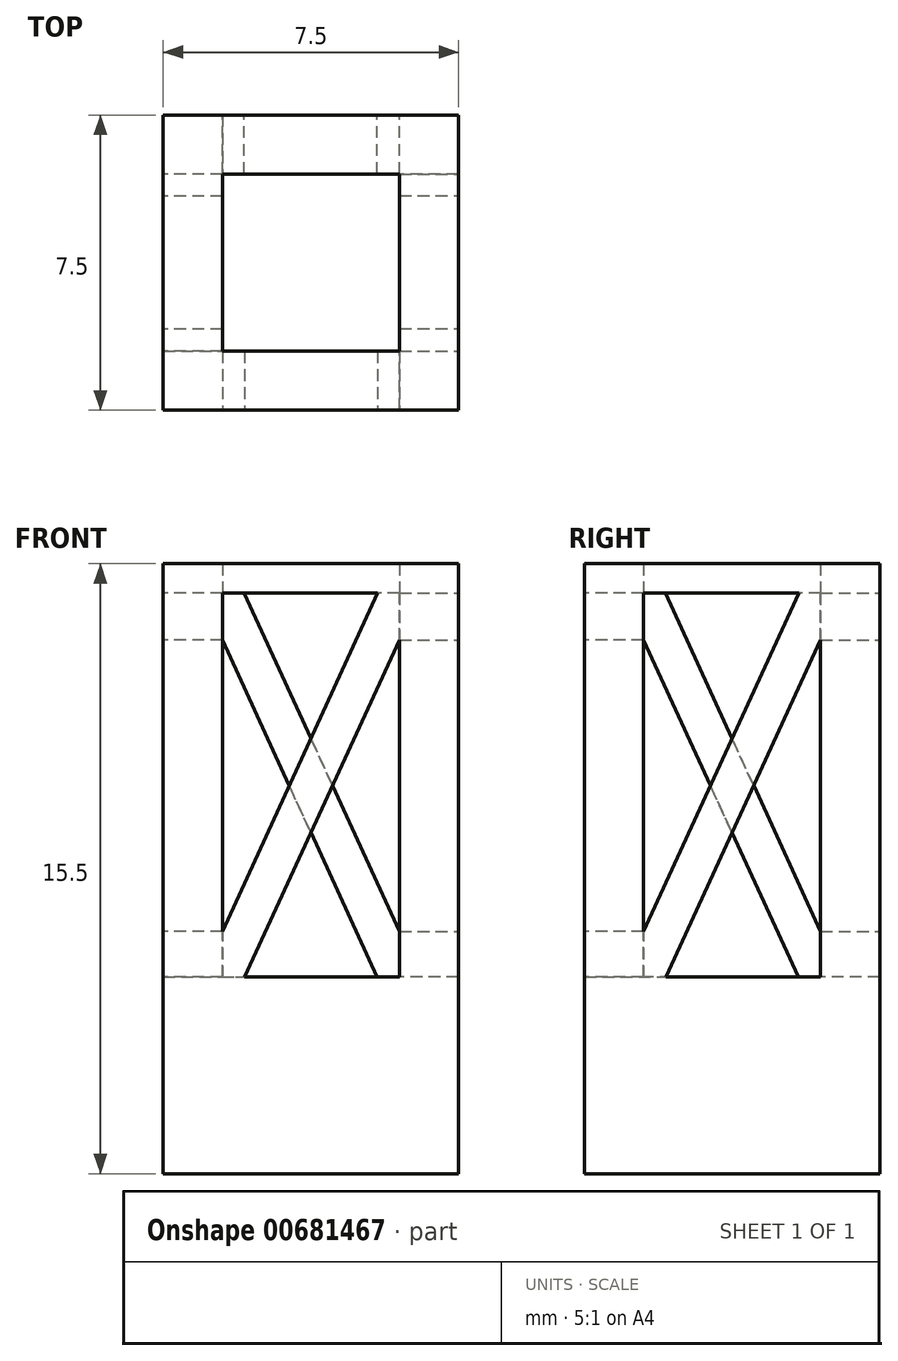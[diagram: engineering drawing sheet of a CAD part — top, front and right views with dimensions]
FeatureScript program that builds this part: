
annotation { "Feature Type Name" : "Feature", "Feature Type Description" : "" }
export const myFeature = defineFeature(function(context is Context, id is Id, definition is map)
    precondition{}
    {
        {
            var Q0;
            Q0=qCreatedBy(makeId("Top.planeOp"),FACE);
            var sketch = newSketch(context, id + "F0", { "sketchPlane" : qUnion([Q0])});
            skLineSegment(sketch, "E0.bottom", {"start": v(-38.75, 50) * mm, "end": v(-31.25, 50) * mm});
            skPoint(sketch, "E0.middle", {"position": v(0, 0) * mm});
            skLineSegment(sketch, "E1.top", {"start": v(-38.75, 42.5) * mm, "end": v(-31.25, 42.5) * mm});
            skLineSegment(sketch, "E1.left", {"start": v(-38.75, 50) * mm, "end": v(-38.75, 42.5) * mm});
            skLineSegment(sketch, "E1.right", {"start": v(-31.25, 50) * mm, "end": v(-31.25, 42.5) * mm});
            skLineSegment(sketch, "E2.bottom", {"start": v(38.75, 50) * mm, "end": v(31.25, 50) * mm});
            skLineSegment(sketch, "E3.trimOffspring", {"start": v(31.25, 50) * mm, "end": v(38.75, 50) * mm});
            skLineSegment(sketch, "E4", {"start": v(-38.75, 50) * mm, "end": v(38.75, 50) * mm});
            skLineSegment(sketch, "E5", {"start": v(-38.75, 50) * mm, "end": v(-38.75, -50) * mm});
            skPoint(sketch, "E5.endSnap0", {"position": v(-38.75, 46.25) * mm});
            skSolve(sketch);
        }
        {
            var Q0;
            {var subQ0=sQuery(id+"F0.wireOp",EDGE,"E1.top");Q0=makeQuery(id+"F0.imprint","IMPRINT",FACE,{"disambiguationData":[TD([[makeQuery(id+"F0.imprint","IMPRINT",EDGE,{"derivedFrom":subQ0}),1.0]])]});}
            extrude(context, id + "F1", {"entities" : qUnion([Q0]), "depth" : 5 * mm, "offsetDistance" : 25 * mm});
        }
        {
            var Q0;
            Q0=makeQuery(id+"F1.opExtrude","CAP_FACE",FACE,{"disambiguationData":[OSD([sQuery(id+"F0.wireOp",EDGE,"E0.bottom"),sQuery(id+"F0.wireOp",EDGE,"E1.top"),sQuery(id+"F0.wireOp",EDGE,"E1.left"),sQuery(id+"F0.wireOp",EDGE,"E1.right")])],"isStart":false});
            var sketch = newSketch(context, id + "F2", { "sketchPlane" : qUnion([Q0])});
            skLineSegment(sketch, "E6.bottom", {"start": v(-38.75, 50) * mm, "end": v(-37.25, 50) * mm});
            skLineSegment(sketch, "E6.top", {"start": v(-38.75, 48.5) * mm, "end": v(-37.25, 48.5) * mm});
            skLineSegment(sketch, "E6.left", {"start": v(-38.75, 50) * mm, "end": v(-38.75, 48.5) * mm});
            skLineSegment(sketch, "E6.right", {"start": v(-37.25, 50) * mm, "end": v(-37.25, 48.5) * mm});
            skLineSegment(sketch, "E7.bottom", {"start": v(-31.25, 42.5) * mm, "end": v(-32.75, 42.5) * mm});
            skLineSegment(sketch, "E8.bottom", {"start": v(-38.75, 42.5) * mm, "end": v(-37.25, 42.5) * mm});
            skLineSegment(sketch, "E8.top", {"start": v(-38.75, 44) * mm, "end": v(-37.25, 44) * mm});
            skLineSegment(sketch, "E8.left", {"start": v(-38.75, 42.5) * mm, "end": v(-38.75, 44) * mm});
            skLineSegment(sketch, "E8.right", {"start": v(-37.25, 42.5) * mm, "end": v(-37.25, 44) * mm});
            skLineSegment(sketch, "E9.top", {"start": v(-31.25, 44) * mm, "end": v(-32.75, 44) * mm});
            skLineSegment(sketch, "E9.left", {"start": v(-31.25, 42.5) * mm, "end": v(-31.25, 44) * mm});
            skLineSegment(sketch, "E9.right", {"start": v(-32.75, 42.5) * mm, "end": v(-32.75, 44) * mm});
            skLineSegment(sketch, "E10.bottom", {"start": v(-31.25, 50) * mm, "end": v(-32.75, 50) * mm});
            skLineSegment(sketch, "E10.top", {"start": v(-31.25, 48.5) * mm, "end": v(-32.75, 48.5) * mm});
            skLineSegment(sketch, "E10.left", {"start": v(-31.25, 50) * mm, "end": v(-31.25, 48.5) * mm});
            skLineSegment(sketch, "E10.right", {"start": v(-32.75, 50) * mm, "end": v(-32.75, 48.5) * mm});
            skSolve(sketch);
        }
        {
            var Q0;
            Q0=qSketchRegion(id+"F2",true);
            extrude(context, id + "F3", {"entities" : qUnion([Q0]), "operationType" : NewBodyOperationType.ADD, "depth" : 45 * mm, "offsetDistance" : 25 * mm});
        }
        {
            var Q0;
            Q0=makeQuery(id+"F3.opExtrude","CAP_FACE",FACE,{"disambiguationData":[OSD([sQuery(id+"F2.wireOp",EDGE,"E6.bottom"),sQuery(id+"F2.wireOp",EDGE,"E6.top"),sQuery(id+"F2.wireOp",EDGE,"E6.left"),sQuery(id+"F2.wireOp",EDGE,"E6.right")])],"isStart":false});
            var sketch = newSketch(context, id + "F4", { "sketchPlane" : qUnion([Q0])});
            skLineSegment(sketch, "E11.bottom", {"start": v(-38.75, 50) * mm, "end": v(-31.25, 50) * mm});
            skLineSegment(sketch, "E11.top", {"start": v(-38.75, 42.5) * mm, "end": v(-31.25, 42.5) * mm});
            skLineSegment(sketch, "E11.left", {"start": v(-38.75, 50) * mm, "end": v(-38.75, 42.5) * mm});
            skLineSegment(sketch, "E11.right", {"start": v(-31.25, 50) * mm, "end": v(-31.25, 42.5) * mm});
            skSolve(sketch);
        }
        {
            var Q0;
            Q0=qSketchRegion(id+"F4",true);
            extrude(context, id + "F5", {"entities" : qUnion([Q0]), "operationType" : NewBodyOperationType.ADD, "depth" : 5 * mm, "offsetDistance" : 25 * mm});
        }
        {
            var Q0;
            Q0=makeQuery(id+"F5.boolean.opBoolean","MERGE",FACE,{"derivedFrom":[makeQuery(id+"F3.boolean.opBoolean","MERGE",FACE,{"derivedFrom":[makeQuery(id+"F1.opExtrude","SWEPT_FACE",FACE,{"disambiguationData":[OSD([sQuery(id+"F0.wireOp",EDGE,"E1.left")])]}),makeQuery(id+"F3.opExtrude","SWEPT_FACE",FACE,{"disambiguationData":[OSD([sQuery(id+"F2.wireOp",EDGE,"E6.left")])]}),makeQuery(id+"F3.opExtrude","SWEPT_FACE",FACE,{"disambiguationData":[OSD([sQuery(id+"F2.wireOp",EDGE,"E8.left")])]})]}),makeQuery(id+"F5.opExtrude","SWEPT_FACE",FACE,{"disambiguationData":[OSD([sQuery(id+"F4.wireOp",EDGE,"E11.left")])]})]});
            var sketch = newSketch(context, id + "F6", { "sketchPlane" : qUnion([Q0])});
            skLineSegment(sketch, "E12", {"start": v(-48.5, 5) * mm, "end": v(-48.5, 14.75) * mm});
            skLineSegment(sketch, "E13", {"start": v(-48.5, 14.75) * mm, "end": v(-48.5, 16.75) * mm});
            skLineSegment(sketch, "E14", {"start": v(-48.5, 16.75) * mm, "end": v(-48.5, 26.5) * mm});
            skLineSegment(sketch, "E15", {"start": v(-48.5, 26.5) * mm, "end": v(-48.5, 28.5) * mm});
            skLineSegment(sketch, "E16", {"start": v(-48.5, 28.5) * mm, "end": v(-48.5, 38.25) * mm});
            skLineSegment(sketch, "E17", {"start": v(-48.5, 38.25) * mm, "end": v(-48.5, 40.25) * mm});
            skLineSegment(sketch, "E18", {"start": v(-48.5, 40.25) * mm, "end": v(-48.5, 50) * mm});
            skLineSegment(sketch, "E19", {"start": v(-48.5, 40.25) * mm, "end": v(-44.57, 40.25) * mm});
            skLineSegment(sketch, "E20", {"start": v(-48.5, 38.25) * mm, "end": v(-44.55, 38.25) * mm});
            skLineSegment(sketch, "E21", {"start": v(-47.96, 28.5) * mm, "end": v(-44, 28.5) * mm});
            skLineSegment(sketch, "E22", {"start": v(-48.5, 26.5) * mm, "end": v(-48.49, 26.5) * mm});
            skLineSegment(sketch, "E23", {"start": v(-48.5, 16.75) * mm, "end": v(-44.58, 16.75) * mm});
            skLineSegment(sketch, "E24", {"start": v(-48.5, 14.75) * mm, "end": v(-44.55, 14.75) * mm});
            skLineSegment(sketch, "E25.bottom", {"start": v(-48.5, 6.16) * mm, "end": v(-44.4, 15.08) * mm});
            skLineSegment(sketch, "E25.top", {"start": v(-47.93, 5) * mm, "end": v(-43.5, 14.66) * mm});
            skLineSegment(sketch, "E25.right", {"start": v(-44, 14.9) * mm, "end": v(-43.5, 14.66) * mm});
            skLineSegment(sketch, "E26", {"start": v(-43.95, 14.87) * mm, "end": v(-44, 14.76) * mm});
            skLineSegment(sketch, "E27.bottom", {"start": v(-44.45, 16.47) * mm, "end": v(-49.03, 26.47) * mm});
            skLineSegment(sketch, "E27.top", {"start": v(-43.54, 16.89) * mm, "end": v(-47.94, 26.5) * mm});
            skLineSegment(sketch, "E27.left", {"start": v(-44, 16.67) * mm, "end": v(-43.54, 16.89) * mm});
            skLineSegment(sketch, "E27.right", {"start": v(-48.57, 26.68) * mm, "end": v(-48.12, 26.89) * mm});
            skLineSegment(sketch, "E28", {"start": v(-44, 16.68) * mm, "end": v(-44, 16.7) * mm});
            skLineSegment(sketch, "E29", {"start": v(-48.57, 26.68) * mm, "end": v(-47.42, 24.16) * mm});
            skLineSegment(sketch, "E30.bottom", {"start": v(-49.02, 28.6) * mm, "end": v(-44.55, 38.25) * mm});
            skLineSegment(sketch, "E30.top", {"start": v(-47.96, 28.5) * mm, "end": v(-43.5, 38.16) * mm});
            skLineSegment(sketch, "E30.left", {"start": v(-49.02, 28.6) * mm, "end": v(-48.1, 28.18) * mm});
            skLineSegment(sketch, "E30.right", {"start": v(-44.4, 38.58) * mm, "end": v(-43.5, 38.16) * mm});
            skLineSegment(sketch, "E31", {"start": v(-48.56, 28.39) * mm, "end": v(-47.84, 29.96) * mm});
            skLineSegment(sketch, "E32", {"start": v(-43.94, 38.37) * mm, "end": v(-45.1, 35.86) * mm});
            skLineSegment(sketch, "E33.bottom", {"start": v(-44.43, 39.92) * mm, "end": v(-49, 49.93) * mm});
            skLineSegment(sketch, "E33.top", {"start": v(-43.52, 40.34) * mm, "end": v(-48.1, 50.34) * mm});
            skLineSegment(sketch, "E33.left", {"start": v(-44, 40.12) * mm, "end": v(-43.52, 40.34) * mm});
            skLineSegment(sketch, "E33.right", {"start": v(-49, 49.93) * mm, "end": v(-48.1, 50.34) * mm});
            skLineSegment(sketch, "E34", {"start": v(-43.97, 40.13) * mm, "end": v(-44, 40.2) * mm});
            skLineSegment(sketch, "E35", {"start": v(-48.55, 50.13) * mm, "end": v(-47.4, 47.62) * mm});
            skLineSegment(sketch, "E36", {"start": v(-44, 5) * mm, "end": v(-44, 14.75) * mm});
            skLineSegment(sketch, "E37", {"start": v(-48.5, 5) * mm, "end": v(-44, 5) * mm});
            skLineSegment(sketch, "E38.trimOffspring", {"start": v(-44.03, 16.75) * mm, "end": v(-44.71, 18.25) * mm});
            skLineSegment(sketch, "E39.trimOffspring", {"start": v(-44, 14.76) * mm, "end": v(-44, 50) * mm});
            skLineSegment(sketch, "E40.trimOffspring", {"start": v(-44, 14.75) * mm, "end": v(-45.1, 12.35) * mm});
            skLineSegment(sketch, "E41.trimOffspring", {"start": v(-44.02, 40.25) * mm, "end": v(-44.7, 41.7) * mm});
            skLineSegment(sketch, "E42.trimOffspring", {"start": v(-44, 14.75) * mm, "end": v(-44, 14.75) * mm});
            skLineSegment(sketch, "E43.trimOffspring", {"start": v(-44.03, 16.75) * mm, "end": v(-44, 16.75) * mm});
            skLineSegment(sketch, "E44.trimOffspring", {"start": v(-47.94, 26.5) * mm, "end": v(-44, 26.5) * mm});
            skLineSegment(sketch, "E45.trimOffspring", {"start": v(-44, 38.25) * mm, "end": v(-44, 38.25) * mm});
            skLineSegment(sketch, "E46.trimOffspring", {"start": v(-44.02, 40.25) * mm, "end": v(-44, 40.25) * mm});
            skLineSegment(sketch, "E47", {"start": v(-48.5, 6.16) * mm, "end": v(-48.5, 5) * mm});
            skLineSegment(sketch, "E48", {"start": v(-48.5, 5) * mm, "end": v(-47.93, 5) * mm});
            skSolve(sketch);
        }
        {
            var Q0;
            {var subQ0=sQuery(id+"F6.wireOp",EDGE,"978fa180-220d-49b5-a42c-c1bf2bef534437.MirrorCS");var subQ1=sQuery(id+"F6.wireOp",EDGE,"978fa180-220d-49b5-a42c-c1bf2bef53440.MirrorCS");var subQ2=makeQuery(id+"F6.imprint","INTERSECT",VERTEX,{"derivedFrom":[subQ1,subQ0]});Q0=makeQuery(id+"F6.imprint","IMPRINT",FACE,{"disambiguationData":[TD([[makeQuery(id+"F6.imprint","IMPRINT",EDGE,{"disambiguationData":[TD([[subQ2,-1.0]])],"derivedFrom":subQ1}),-1.0]])]});}
            var Q1;
            {var subQ0=sQuery(id+"F6.wireOp",EDGE,"978fa180-220d-49b5-a42c-c1bf2bef534428.MirrorCS");var subQ1=sQuery(id+"F6.wireOp",EDGE,"978fa180-220d-49b5-a42c-c1bf2bef53442.MirrorCS");var subQ2=makeQuery(id+"F6.imprint","INTERSECT",VERTEX,{"derivedFrom":[subQ1,subQ0]});Q1=makeQuery(id+"F6.imprint","IMPRINT",FACE,{"disambiguationData":[TD([[makeQuery(id+"F6.imprint","IMPRINT",EDGE,{"disambiguationData":[TD([[subQ2,-1.0]])],"derivedFrom":subQ1}),-1.0]])]});}
            var Q2;
            {var subQ0=sQuery(id+"F6.wireOp",EDGE,"978fa180-220d-49b5-a42c-c1bf2bef534432.MirrorCS");var subQ1=sQuery(id+"F6.wireOp",EDGE,"978fa180-220d-49b5-a42c-c1bf2bef53443.MirrorCS");var subQ2=makeQuery(id+"F6.imprint","INTERSECT",VERTEX,{"derivedFrom":[subQ1,subQ0]});Q2=makeQuery(id+"F6.imprint","IMPRINT",FACE,{"disambiguationData":[TD([[makeQuery(id+"F6.imprint","IMPRINT",EDGE,{"disambiguationData":[TD([[subQ2,-1.0]])],"derivedFrom":subQ1}),1.0]])]});}
            var Q3;
            {var subQ0=sQuery(id+"F6.wireOp",EDGE,"978fa180-220d-49b5-a42c-c1bf2bef534429.MirrorCS");var subQ1=sQuery(id+"F6.wireOp",EDGE,"978fa180-220d-49b5-a42c-c1bf2bef53444.MirrorCS");var subQ2=makeQuery(id+"F6.imprint","INTERSECT",VERTEX,{"derivedFrom":[subQ1,subQ0]});Q3=makeQuery(id+"F6.imprint","IMPRINT",FACE,{"disambiguationData":[TD([[makeQuery(id+"F6.imprint","IMPRINT",EDGE,{"disambiguationData":[TD([[subQ2,-1.0]])],"derivedFrom":subQ1}),-1.0]])]});}
            var Q4;
            {var subQ0=sQuery(id+"F6.wireOp",EDGE,"978fa180-220d-49b5-a42c-c1bf2bef534435.MirrorCS");var subQ1=sQuery(id+"F6.wireOp",EDGE,"978fa180-220d-49b5-a42c-c1bf2bef53446.MirrorCS");var subQ2=makeQuery(id+"F6.imprint","INTERSECT",VERTEX,{"derivedFrom":[subQ1,subQ0]});Q4=makeQuery(id+"F6.imprint","IMPRINT",FACE,{"disambiguationData":[TD([[makeQuery(id+"F6.imprint","IMPRINT",EDGE,{"disambiguationData":[TD([[subQ2,-1.0]])],"derivedFrom":subQ1}),1.0]])]});}
            var Q5;
            {var subQ0=sQuery(id+"F6.wireOp",EDGE,"978fa180-220d-49b5-a42c-c1bf2bef534431.MirrorCS");var subQ1=sQuery(id+"F6.wireOp",EDGE,"978fa180-220d-49b5-a42c-c1bf2bef53447.MirrorCS");var subQ2=makeQuery(id+"F6.imprint","INTERSECT",VERTEX,{"derivedFrom":[subQ1,subQ0]});Q5=makeQuery(id+"F6.imprint","IMPRINT",FACE,{"disambiguationData":[TD([[makeQuery(id+"F6.imprint","IMPRINT",EDGE,{"disambiguationData":[TD([[subQ2,-1.0]])],"derivedFrom":subQ1}),-1.0]])]});}
            var Q6;
            {var subQ3=sQuery(id+"F6.wireOp",EDGE,"E30.left");var subQ5=sQuery(id+"F6.wireOp",EDGE,"E30.top");var subQ6=makeQuery(id+"F6.imprint","INTERSECT",VERTEX,{"derivedFrom":[subQ5,subQ3]});Q6=makeQuery(id+"F6.imprint","IMPRINT",FACE,{"disambiguationData":[TD([[makeQuery(id+"F6.imprint","IMPRINT",EDGE,{"disambiguationData":[TD([[subQ6,-1.0]])],"derivedFrom":subQ5}),1.0]])]});}
            var Q7;
            {var subQ0=sQuery(id+"F6.wireOp",EDGE,"E27.right");var subQ1=sQuery(id+"F6.wireOp",EDGE,"E15");var subQ2=makeQuery(id+"F6.imprint","INTERSECT",VERTEX,{"derivedFrom":[subQ1,subQ0]});Q7=makeQuery(id+"F6.imprint","IMPRINT",FACE,{"disambiguationData":[TD([[makeQuery(id+"F6.imprint","IMPRINT",EDGE,{"disambiguationData":[TD([[subQ2,-1.0]])],"derivedFrom":subQ1}),-1.0]])]});}
            var Q8;
            {var subQ0=sQuery(id+"F6.wireOp",EDGE,"E31");var subQ1=sQuery(id+"F6.wireOp",EDGE,"E16");var subQ2=makeQuery(id+"F6.imprint","INTERSECT",VERTEX,{"derivedFrom":[subQ1,subQ0]});Q8=makeQuery(id+"F6.imprint","IMPRINT",FACE,{"disambiguationData":[TD([[makeQuery(id+"F6.imprint","IMPRINT",EDGE,{"disambiguationData":[TD([[subQ2,1.0]])],"derivedFrom":subQ1}),-1.0]])]});}
            var Q9;
            {var subQ0=sQuery(id+"F6.wireOp",EDGE,"E26");var subQ1=sQuery(id+"F6.wireOp",EDGE,"E25.right");var subQ2=makeQuery(id+"F6.imprint","INTERSECT",VERTEX,{"derivedFrom":[subQ1,subQ0]});Q9=makeQuery(id+"F6.imprint","IMPRINT",FACE,{"disambiguationData":[TD([[makeQuery(id+"F6.imprint","IMPRINT",EDGE,{"disambiguationData":[TD([[subQ2,1.0]])],"derivedFrom":subQ1}),-1.0]])]});}
            var Q10;
            {var subQ0=sQuery(id+"F6.wireOp",EDGE,"E28");var subQ1=sQuery(id+"F6.wireOp",EDGE,"E27.left");var subQ2=makeQuery(id+"F6.imprint","INTERSECT",VERTEX,{"derivedFrom":[subQ1,subQ0]});Q10=makeQuery(id+"F6.imprint","IMPRINT",FACE,{"disambiguationData":[TD([[makeQuery(id+"F6.imprint","IMPRINT",EDGE,{"disambiguationData":[TD([[subQ2,1.0]])],"derivedFrom":subQ1}),1.0]])]});}
            var Q11;
            {var subQ0=sQuery(id+"F6.wireOp",EDGE,"E32");var subQ1=sQuery(id+"F6.wireOp",EDGE,"E30.right");var subQ2=makeQuery(id+"F6.imprint","INTERSECT",VERTEX,{"derivedFrom":[subQ1,subQ0]});Q11=makeQuery(id+"F6.imprint","IMPRINT",FACE,{"disambiguationData":[TD([[makeQuery(id+"F6.imprint","IMPRINT",EDGE,{"disambiguationData":[TD([[subQ2,1.0]])],"derivedFrom":subQ1}),-1.0]])]});}
            var Q12;
            {var subQ0=sQuery(id+"F6.wireOp",EDGE,"E34");var subQ1=sQuery(id+"F6.wireOp",EDGE,"E33.left");var subQ2=makeQuery(id+"F6.imprint","INTERSECT",VERTEX,{"derivedFrom":[subQ1,subQ0]});Q12=makeQuery(id+"F6.imprint","IMPRINT",FACE,{"disambiguationData":[TD([[makeQuery(id+"F6.imprint","IMPRINT",EDGE,{"disambiguationData":[TD([[subQ2,1.0]])],"derivedFrom":subQ1}),1.0]])]});}
            var Q13;
            {var subQ0=sQuery(id+"F6.wireOp",EDGE,"978fa180-220d-49b5-a42c-c1bf2bef534437.MirrorCS");var subQ6=sQuery(id+"F6.wireOp",EDGE,"978fa180-220d-49b5-a42c-c1bf2bef53440.MirrorCS");var subQ8=makeQuery(id+"F6.imprint","INTERSECT",VERTEX,{"derivedFrom":[subQ6,subQ0]});Q13=makeQuery(id+"F6.imprint","IMPRINT",FACE,{"disambiguationData":[TD([[makeQuery(id+"F6.imprint","IMPRINT",EDGE,{"disambiguationData":[TD([[subQ8,-1.0]])],"derivedFrom":subQ6}),1.0]])]});}
            var Q14;
            {var subQ0=sQuery(id+"F6.wireOp",EDGE,"978fa180-220d-49b5-a42c-c1bf2bef534428.MirrorCS");var subQ1=sQuery(id+"F6.wireOp",EDGE,"978fa180-220d-49b5-a42c-c1bf2bef53442.MirrorCS");var subQ2=makeQuery(id+"F6.imprint","INTERSECT",VERTEX,{"derivedFrom":[subQ1,subQ0]});Q14=makeQuery(id+"F6.imprint","IMPRINT",FACE,{"disambiguationData":[TD([[makeQuery(id+"F6.imprint","IMPRINT",EDGE,{"disambiguationData":[TD([[subQ2,-1.0]])],"derivedFrom":subQ1}),1.0]])]});}
            var Q15;
            {var subQ2=sQuery(id+"F6.wireOp",EDGE,"978fa180-220d-49b5-a42c-c1bf2bef53443.MirrorCS");var subQ4=sQuery(id+"F6.wireOp",EDGE,"978fa180-220d-49b5-a42c-c1bf2bef534432.MirrorCS");var subQ8=makeQuery(id+"F6.imprint","INTERSECT",VERTEX,{"derivedFrom":[subQ2,subQ4]});Q15=makeQuery(id+"F6.imprint","IMPRINT",FACE,{"disambiguationData":[TD([[makeQuery(id+"F6.imprint","IMPRINT",EDGE,{"disambiguationData":[TD([[subQ8,-1.0]])],"derivedFrom":subQ2}),-1.0]])]});}
            var Q16;
            {var subQ3=sQuery(id+"F6.wireOp",EDGE,"978fa180-220d-49b5-a42c-c1bf2bef53444.MirrorCS");var subQ5=sQuery(id+"F6.wireOp",EDGE,"978fa180-220d-49b5-a42c-c1bf2bef534429.MirrorCS");var subQ9=makeQuery(id+"F6.imprint","INTERSECT",VERTEX,{"derivedFrom":[subQ3,subQ5]});Q16=makeQuery(id+"F6.imprint","IMPRINT",FACE,{"disambiguationData":[TD([[makeQuery(id+"F6.imprint","IMPRINT",EDGE,{"disambiguationData":[TD([[subQ9,-1.0]])],"derivedFrom":subQ3}),1.0]])]});}
            var Q17;
            {var subQ2=sQuery(id+"F6.wireOp",EDGE,"978fa180-220d-49b5-a42c-c1bf2bef53446.MirrorCS");var subQ4=sQuery(id+"F6.wireOp",EDGE,"978fa180-220d-49b5-a42c-c1bf2bef534435.MirrorCS");var subQ8=makeQuery(id+"F6.imprint","INTERSECT",VERTEX,{"derivedFrom":[subQ2,subQ4]});Q17=makeQuery(id+"F6.imprint","IMPRINT",FACE,{"disambiguationData":[TD([[makeQuery(id+"F6.imprint","IMPRINT",EDGE,{"disambiguationData":[TD([[subQ8,-1.0]])],"derivedFrom":subQ2}),-1.0]])]});}
            var Q18;
            {var subQ0=sQuery(id+"F6.wireOp",EDGE,"978fa180-220d-49b5-a42c-c1bf2bef534431.MirrorCS");var subQ6=sQuery(id+"F6.wireOp",EDGE,"978fa180-220d-49b5-a42c-c1bf2bef53447.MirrorCS");var subQ8=makeQuery(id+"F6.imprint","INTERSECT",VERTEX,{"derivedFrom":[subQ6,subQ0]});Q18=makeQuery(id+"F6.imprint","IMPRINT",FACE,{"disambiguationData":[TD([[makeQuery(id+"F6.imprint","IMPRINT",EDGE,{"disambiguationData":[TD([[subQ8,-1.0]])],"derivedFrom":subQ6}),1.0]])]});}
            var Q19;
            {var subQ0=sQuery(id+"F6.wireOp",EDGE,"978fa180-220d-49b5-a42c-c1bf2bef534428.MirrorCS");var subQ1=sQuery(id+"F6.wireOp",EDGE,"978fa180-220d-49b5-a42c-c1bf2bef53449.MirrorCS");var subQ2=makeQuery(id+"F6.imprint","INTERSECT",VERTEX,{"derivedFrom":[subQ1,subQ0]});Q19=makeQuery(id+"F6.imprint","IMPRINT",FACE,{"disambiguationData":[TD([[makeQuery(id+"F6.imprint","IMPRINT",EDGE,{"disambiguationData":[TD([[subQ2,-1.0]])],"derivedFrom":subQ1}),-1.0]])]});}
            var Q20;
            {var subQ0=sQuery(id+"F6.wireOp",EDGE,"E27.right");var subQ1=sQuery(id+"F6.wireOp",EDGE,"E27.bottom");var subQ2=makeQuery(id+"F6.imprint","INTERSECT",VERTEX,{"derivedFrom":[subQ1,subQ0]});Q20=makeQuery(id+"F6.imprint","IMPRINT",FACE,{"disambiguationData":[TD([[makeQuery(id+"F6.imprint","IMPRINT",EDGE,{"disambiguationData":[TD([[subQ2,1.0]])],"derivedFrom":subQ1}),-1.0]])]});}
            var Q21;
            {var subQ3=sQuery(id+"F6.wireOp",EDGE,"E30.left");var subQ5=sQuery(id+"F6.wireOp",EDGE,"E31");var subQ7=makeQuery(id+"F6.imprint","INTERSECT",VERTEX,{"derivedFrom":[subQ3,subQ5]});Q21=makeQuery(id+"F6.imprint","IMPRINT",FACE,{"disambiguationData":[TD([[makeQuery(id+"F6.imprint","IMPRINT",EDGE,{"disambiguationData":[TD([[subQ7,-1.0]])],"derivedFrom":subQ3}),1.0]])]});}
            var Q22;
            {var subQ0=sQuery(id+"F6.wireOp",EDGE,"E27.right");var subQ5=sQuery(id+"F6.wireOp",EDGE,"E15");var subQ6=makeQuery(id+"F6.imprint","INTERSECT",VERTEX,{"derivedFrom":[subQ5,subQ0]});Q22=makeQuery(id+"F6.imprint","IMPRINT",FACE,{"disambiguationData":[TD([[makeQuery(id+"F6.imprint","IMPRINT",EDGE,{"disambiguationData":[TD([[subQ6,-1.0]])],"derivedFrom":subQ5}),1.0]])]});}
            var Q23;
            {var subQ0=sQuery(id+"F6.wireOp",EDGE,"E34");var subQ1=sQuery(id+"F6.wireOp",EDGE,"E19");var subQ2=makeQuery(id+"F6.imprint","INTERSECT",VERTEX,{"derivedFrom":[subQ1,subQ0]});Q23=makeQuery(id+"F6.imprint","IMPRINT",FACE,{"disambiguationData":[TD([[makeQuery(id+"F6.imprint","IMPRINT",EDGE,{"disambiguationData":[TD([[subQ2,1.0]])],"derivedFrom":subQ1}),-1.0]])]});}
            var Q24;
            {var subQ0=sQuery(id+"F6.wireOp",EDGE,"E32");var subQ1=sQuery(id+"F6.wireOp",EDGE,"E20");var subQ2=makeQuery(id+"F6.imprint","INTERSECT",VERTEX,{"derivedFrom":[subQ1,subQ0]});Q24=makeQuery(id+"F6.imprint","IMPRINT",FACE,{"disambiguationData":[TD([[makeQuery(id+"F6.imprint","IMPRINT",EDGE,{"disambiguationData":[TD([[subQ2,1.0]])],"derivedFrom":subQ1}),1.0]])]});}
            var Q25;
            {var subQ0=sQuery(id+"F6.wireOp",EDGE,"E28");var subQ1=sQuery(id+"F6.wireOp",EDGE,"E23");var subQ2=makeQuery(id+"F6.imprint","INTERSECT",VERTEX,{"derivedFrom":[subQ1,subQ0]});Q25=makeQuery(id+"F6.imprint","IMPRINT",FACE,{"disambiguationData":[TD([[makeQuery(id+"F6.imprint","IMPRINT",EDGE,{"disambiguationData":[TD([[subQ2,1.0]])],"derivedFrom":subQ1}),-1.0]])]});}
            var Q26;
            {var subQ3=sQuery(id+"F6.wireOp",EDGE,"E24");var subQ5=sQuery(id+"F6.wireOp",EDGE,"E26");var subQ6=makeQuery(id+"F6.imprint","INTERSECT",VERTEX,{"derivedFrom":[subQ3,subQ5]});Q26=makeQuery(id+"F6.imprint","IMPRINT",FACE,{"disambiguationData":[TD([[makeQuery(id+"F6.imprint","IMPRINT",EDGE,{"disambiguationData":[TD([[subQ6,1.0]])],"derivedFrom":subQ3}),1.0]])]});}
            var Q27;
            {var subQ1=sQuery(id+"F6.wireOp",EDGE,"E25.right");var subQ6=sQuery(id+"F6.wireOp",EDGE,"E25.top");var subQ7=makeQuery(id+"F6.imprint","INTERSECT",VERTEX,{"derivedFrom":[subQ6,subQ1]});Q27=makeQuery(id+"F6.imprint","IMPRINT",FACE,{"disambiguationData":[TD([[makeQuery(id+"F6.imprint","IMPRINT",EDGE,{"disambiguationData":[TD([[subQ7,1.0]])],"derivedFrom":subQ6}),1.0]])]});}
            var Q28;
            {var subQ2=sQuery(id+"F6.wireOp",EDGE,"E27.top");var subQ5=sQuery(id+"F6.wireOp",EDGE,"E27.left");var subQ8=makeQuery(id+"F6.imprint","INTERSECT",VERTEX,{"derivedFrom":[subQ2,subQ5]});Q28=makeQuery(id+"F6.imprint","IMPRINT",FACE,{"disambiguationData":[TD([[makeQuery(id+"F6.imprint","IMPRINT",EDGE,{"disambiguationData":[TD([[subQ8,-1.0]])],"derivedFrom":subQ2}),1.0]])]});}
            var Q29;
            {var subQ1=sQuery(id+"F6.wireOp",EDGE,"E30.right");var subQ6=sQuery(id+"F6.wireOp",EDGE,"E30.top");var subQ7=makeQuery(id+"F6.imprint","INTERSECT",VERTEX,{"derivedFrom":[subQ6,subQ1]});Q29=makeQuery(id+"F6.imprint","IMPRINT",FACE,{"disambiguationData":[TD([[makeQuery(id+"F6.imprint","IMPRINT",EDGE,{"disambiguationData":[TD([[subQ7,1.0]])],"derivedFrom":subQ6}),1.0]])]});}
            var Q30;
            {var subQ2=sQuery(id+"F6.wireOp",EDGE,"E33.top");var subQ5=sQuery(id+"F6.wireOp",EDGE,"E33.left");var subQ8=makeQuery(id+"F6.imprint","INTERSECT",VERTEX,{"derivedFrom":[subQ2,subQ5]});Q30=makeQuery(id+"F6.imprint","IMPRINT",FACE,{"disambiguationData":[TD([[makeQuery(id+"F6.imprint","IMPRINT",EDGE,{"disambiguationData":[TD([[subQ8,-1.0]])],"derivedFrom":subQ2}),1.0]])]});}
            var Q31;
            {var subQ3=sQuery(id+"F6.wireOp",EDGE,"978fa180-220d-49b5-a42c-c1bf2bef534415.MirrorCS");var subQ5=sQuery(id+"F6.wireOp",EDGE,"978fa180-220d-49b5-a42c-c1bf2bef53440.MirrorCS");var subQ6=makeQuery(id+"F6.imprint","INTERSECT",VERTEX,{"derivedFrom":[subQ5,subQ3]});Q31=makeQuery(id+"F6.imprint","IMPRINT",FACE,{"disambiguationData":[TD([[makeQuery(id+"F6.imprint","IMPRINT",EDGE,{"disambiguationData":[TD([[subQ6,1.0]])],"derivedFrom":subQ5}),-1.0]])]});}
            var Q32;
            {var subQ3=sQuery(id+"F6.wireOp",EDGE,"978fa180-220d-49b5-a42c-c1bf2bef534416.MirrorCS");var subQ7=sQuery(id+"F6.wireOp",EDGE,"978fa180-220d-49b5-a42c-c1bf2bef53443.MirrorCS");var subQ9=makeQuery(id+"F6.imprint","INTERSECT",VERTEX,{"derivedFrom":[subQ7,subQ3]});Q32=makeQuery(id+"F6.imprint","IMPRINT",FACE,{"disambiguationData":[TD([[makeQuery(id+"F6.imprint","IMPRINT",EDGE,{"disambiguationData":[TD([[subQ9,1.0]])],"derivedFrom":subQ7}),1.0]])]});}
            var Q33;
            {var subQ3=sQuery(id+"F6.wireOp",EDGE,"978fa180-220d-49b5-a42c-c1bf2bef53444.MirrorCS");var subQ7=sQuery(id+"F6.wireOp",EDGE,"978fa180-220d-49b5-a42c-c1bf2bef534419.MirrorCS");var subQ9=makeQuery(id+"F6.imprint","INTERSECT",VERTEX,{"derivedFrom":[subQ3,subQ7]});Q33=makeQuery(id+"F6.imprint","IMPRINT",FACE,{"disambiguationData":[TD([[makeQuery(id+"F6.imprint","IMPRINT",EDGE,{"disambiguationData":[TD([[subQ9,1.0]])],"derivedFrom":subQ3}),-1.0]])]});}
            var Q34;
            {var subQ0=sQuery(id+"F6.wireOp",EDGE,"978fa180-220d-49b5-a42c-c1bf2bef534425.MirrorCS");var subQ1=sQuery(id+"F6.wireOp",EDGE,"978fa180-220d-49b5-a42c-c1bf2bef53446.MirrorCS");var subQ2=makeQuery(id+"F6.imprint","INTERSECT",VERTEX,{"derivedFrom":[subQ1,subQ0]});Q34=makeQuery(id+"F6.imprint","IMPRINT",FACE,{"disambiguationData":[TD([[makeQuery(id+"F6.imprint","IMPRINT",EDGE,{"disambiguationData":[TD([[subQ2,1.0]])],"derivedFrom":subQ1}),1.0]])]});}
            var Q35;
            {var subQ0=sQuery(id+"F6.wireOp",EDGE,"978fa180-220d-49b5-a42c-c1bf2bef534421.MirrorCS");var subQ1=sQuery(id+"F6.wireOp",EDGE,"978fa180-220d-49b5-a42c-c1bf2bef53447.MirrorCS");var subQ2=makeQuery(id+"F6.imprint","INTERSECT",VERTEX,{"derivedFrom":[subQ1,subQ0]});Q35=makeQuery(id+"F6.imprint","IMPRINT",FACE,{"disambiguationData":[TD([[makeQuery(id+"F6.imprint","IMPRINT",EDGE,{"disambiguationData":[TD([[subQ2,1.0]])],"derivedFrom":subQ1}),-1.0]])]});}
            var Q36;
            {var subQ3=sQuery(id+"F6.wireOp",EDGE,"978fa180-220d-49b5-a42c-c1bf2bef53449.MirrorCS");var subQ13=sQuery(id+"F6.wireOp",EDGE,"978fa180-220d-49b5-a42c-c1bf2bef534428.MirrorCS");var subQ14=makeQuery(id+"F6.imprint","INTERSECT",VERTEX,{"derivedFrom":[subQ3,subQ13]});Q36=makeQuery(id+"F6.imprint","IMPRINT",FACE,{"disambiguationData":[TD([[makeQuery(id+"F6.imprint","IMPRINT",EDGE,{"disambiguationData":[TD([[subQ14,-1.0]])],"derivedFrom":subQ3}),1.0]])]});}
            var Q37;
            {var subQ5=sQuery(id+"F6.wireOp",EDGE,"978fa180-220d-49b5-a42c-c1bf2bef534434.MirrorCS");Q37=makeQuery(id+"F6.imprint","IMPRINT",FACE,{"disambiguationData":[TD([[makeQuery(id+"F6.imprint","IMPRINT",EDGE,{"derivedFrom":subQ5}),1.0]])]});}
            var Q38;
            {var subQ4=sQuery(id+"F6.wireOp",EDGE,"978fa180-220d-49b5-a42c-c1bf2bef534433.MirrorCS");var subQ5=makeQuery(id+"F6.imprint","IMPRINT",VERTEX,{"derivedFrom":subQ4});Q38=makeQuery(id+"F6.imprint","IMPRINT",FACE,{"disambiguationData":[TD([[makeQuery(id+"F6.imprint","IMPRINT",EDGE,{"disambiguationData":[TD([[subQ5,1.0]])],"derivedFrom":subQ4}),-1.0]])]});}
            var Q39;
            {var subQ5=sQuery(id+"F6.wireOp",EDGE,"978fa180-220d-49b5-a42c-c1bf2bef534430.MirrorCS");Q39=makeQuery(id+"F6.imprint","IMPRINT",FACE,{"disambiguationData":[TD([[makeQuery(id+"F6.imprint","IMPRINT",EDGE,{"derivedFrom":subQ5}),1.0]])]});}
            var Q40;
            {var subQ0=sQuery(id+"F6.wireOp",EDGE,"978fa180-220d-49b5-a42c-c1bf2bef534436.MirrorCS");var subQ12=makeQuery(id+"F6.imprint","IMPRINT",VERTEX,{"derivedFrom":subQ0});Q40=makeQuery(id+"F6.imprint","IMPRINT",FACE,{"disambiguationData":[TD([[makeQuery(id+"F6.imprint","IMPRINT",EDGE,{"disambiguationData":[TD([[subQ12,1.0]])],"derivedFrom":subQ0}),1.0]])]});}
            var Q41;
            {var subQ5=sQuery(id+"F6.wireOp",EDGE,"E13");Q41=makeQuery(id+"F6.imprint","IMPRINT",FACE,{"disambiguationData":[TD([[makeQuery(id+"F6.imprint","IMPRINT",EDGE,{"derivedFrom":subQ5}),1.0]])]});}
            var Q42;
            {var subQ11=sQuery(id+"F6.wireOp",EDGE,"E30.left");var subQ12=sQuery(id+"F6.wireOp",EDGE,"E15");var subQ13=makeQuery(id+"F6.imprint","INTERSECT",VERTEX,{"derivedFrom":[subQ12,subQ11]});Q42=makeQuery(id+"F6.imprint","IMPRINT",FACE,{"disambiguationData":[TD([[makeQuery(id+"F6.imprint","IMPRINT",EDGE,{"disambiguationData":[TD([[subQ13,-1.0]])],"derivedFrom":subQ12}),1.0]])]});}
            var Q43;
            {var subQ5=sQuery(id+"F6.wireOp",EDGE,"E17");Q43=makeQuery(id+"F6.imprint","IMPRINT",FACE,{"disambiguationData":[TD([[makeQuery(id+"F6.imprint","IMPRINT",EDGE,{"derivedFrom":subQ5}),1.0]])]});}
            var Q44;
            {var subQ4=sQuery(id+"F6.wireOp",EDGE,"E22");var subQ5=makeQuery(id+"F6.imprint","INTERSECT",VERTEX,{"derivedFrom":[subQ4,sQuery(id+"F6.wireOp",EDGE,"E29")]});Q44=makeQuery(id+"F6.imprint","IMPRINT",FACE,{"disambiguationData":[TD([[makeQuery(id+"F6.imprint","IMPRINT",EDGE,{"disambiguationData":[TD([[subQ5,-1.0]])],"derivedFrom":subQ4}),-1.0]])]});}
            var Q45;
            {var subQ4=sQuery(id+"F6.wireOp",EDGE,"E16");var subQ8=makeQuery(id+"F6.imprint","INTERSECT",VERTEX,{"derivedFrom":[subQ4,sQuery(id+"F6.wireOp",EDGE,"E31")]});Q45=makeQuery(id+"F6.imprint","IMPRINT",FACE,{"disambiguationData":[TD([[makeQuery(id+"F6.imprint","IMPRINT",EDGE,{"disambiguationData":[TD([[subQ8,1.0]])],"derivedFrom":subQ4}),1.0]])]});}
            var Q46;
            {var subQ7=sQuery(id+"F6.wireOp",EDGE,"978fa180-220d-49b5-a42c-c1bf2bef534411.MirrorCS");var subQ8=sQuery(id+"F6.wireOp",EDGE,"978fa180-220d-49b5-a42c-c1bf2bef53448.MirrorCS");var subQ9=makeQuery(id+"F6.imprint","INTERSECT",VERTEX,{"derivedFrom":[subQ8,subQ7]});Q46=makeQuery(id+"F6.imprint","IMPRINT",FACE,{"disambiguationData":[TD([[makeQuery(id+"F6.imprint","IMPRINT",EDGE,{"disambiguationData":[TD([[subQ9,1.0]])],"derivedFrom":subQ7}),1.0]])]});}
            var Q47;
            {var subQ1=sQuery(id+"F6.wireOp",EDGE,"978fa180-220d-49b5-a42c-c1bf2bef534413.MirrorCS");var subQ3=sQuery(id+"F6.wireOp",EDGE,"978fa180-220d-49b5-a42c-c1bf2bef53449.MirrorCS");var subQ4=makeQuery(id+"F6.imprint","INTERSECT",VERTEX,{"derivedFrom":[subQ3,subQ1]});Q47=makeQuery(id+"F6.imprint","IMPRINT",FACE,{"disambiguationData":[TD([[makeQuery(id+"F6.imprint","IMPRINT",EDGE,{"disambiguationData":[TD([[subQ4,1.0]])],"derivedFrom":subQ3}),-1.0]])]});}
            var Q48;
            {var subQ3=makeQuery(id+"F1.opExtrude","CAP_EDGE",EDGE,{"disambiguationData":[OSD([sQuery(id+"F0.wireOp",EDGE,"E1.left")])],"isStart":false});var subQ7=sQuery(id+"F6.wireOp",EDGE,"E12");var subQ9=makeQuery(id+"F6.imprint","INTERSECT",VERTEX,{"derivedFrom":[subQ3,subQ7]});Q48=makeQuery(id+"F6.imprint","IMPRINT",FACE,{"disambiguationData":[TD([[makeQuery(id+"F6.imprint","IMPRINT",EDGE,{"disambiguationData":[TD([[subQ9,1.0]])],"derivedFrom":subQ7}),-1.0]])]});}
            var Q49;
            {var subQ3=makeQuery(id+"F5.opExtrude","CAP_EDGE",EDGE,{"disambiguationData":[OSD([sQuery(id+"F4.wireOp",EDGE,"E11.left")])],"isStart":true});var subQ7=sQuery(id+"F6.wireOp",EDGE,"E18");var subQ9=makeQuery(id+"F6.imprint","INTERSECT",VERTEX,{"derivedFrom":[subQ3,subQ7]});Q49=makeQuery(id+"F6.imprint","IMPRINT",FACE,{"disambiguationData":[TD([[makeQuery(id+"F6.imprint","IMPRINT",EDGE,{"disambiguationData":[TD([[subQ9,-1.0]])],"derivedFrom":subQ7}),-1.0]])]});}
            var Q50;
            {var subQ0=sQuery(id+"F6.wireOp",EDGE,"E25.left");var subQ1=sQuery(id+"F6.wireOp",EDGE,"E25.top");var subQ2=makeQuery(id+"F6.imprint","INTERSECT",VERTEX,{"derivedFrom":[subQ1,subQ0]});Q50=makeQuery(id+"F6.imprint","IMPRINT",FACE,{"disambiguationData":[TD([[makeQuery(id+"F6.imprint","IMPRINT",EDGE,{"disambiguationData":[TD([[subQ2,-1.0]])],"derivedFrom":subQ1}),1.0]])]});}
            var Q51;
            {var subQ0=sQuery(id+"F6.wireOp",EDGE,"E33.right");var subQ1=sQuery(id+"F6.wireOp",EDGE,"E33.top");var subQ2=makeQuery(id+"F6.imprint","INTERSECT",VERTEX,{"derivedFrom":[subQ1,subQ0]});Q51=makeQuery(id+"F6.imprint","IMPRINT",FACE,{"disambiguationData":[TD([[makeQuery(id+"F6.imprint","IMPRINT",EDGE,{"disambiguationData":[TD([[subQ2,1.0]])],"derivedFrom":subQ1}),1.0]])]});}
            var Q52;
            {var subQ6=sQuery(id+"F6.wireOp",EDGE,"E18");var subQ8=makeQuery(id+"F5.opExtrude","CAP_EDGE",EDGE,{"disambiguationData":[OSD([sQuery(id+"F4.wireOp",EDGE,"E11.left")])],"isStart":true});var subQ12=makeQuery(id+"F6.imprint","INTERSECT",VERTEX,{"derivedFrom":[subQ8,subQ6]});Q52=makeQuery(id+"F6.imprint","IMPRINT",FACE,{"disambiguationData":[TD([[makeQuery(id+"F6.imprint","IMPRINT",EDGE,{"disambiguationData":[TD([[subQ12,-1.0]])],"derivedFrom":subQ6}),1.0]])]});}
            var Q53;
            {var subQ35=sQuery(id+"F6.wireOp",EDGE,"a1b9c921-bcd3-4052-8c83-146f9889fe8a2.MirrorCS");Q53=makeQuery(id+"F6.imprint","IMPRINT",FACE,{"disambiguationData":[TD([[makeQuery(id+"F6.imprint","IMPRINT",EDGE,{"derivedFrom":subQ35}),-1.0]])]});}
            extrude(context, id + "F7", {"entities" : qUnion([Q0, Q1, Q2, Q3, Q4, Q5, Q6, Q7, Q8, Q9, Q10, Q11, Q12, Q13, Q14, Q15, Q16, Q17, Q18, Q19, Q20, Q21, Q22, Q23, Q24, Q25, Q26, Q27, Q28, Q29, Q30, Q31, Q32, Q33, Q34, Q35, Q36, Q37, Q38, Q39, Q40, Q41, Q42, Q43, Q44, Q45, Q46, Q47, Q48, Q49, Q50, Q51, Q52, Q53]), "operationType" : NewBodyOperationType.ADD, "oppositeDirection" : true, "depth" : 1.5 * mm, "offsetDistance" : 25 * mm});
        }
        {
            var Q0;
            Q0=makeQuery(id+"F5.boolean.opBoolean","MERGE",FACE,{"derivedFrom":[makeQuery(id+"F3.boolean.opBoolean","MERGE",FACE,{"derivedFrom":[makeQuery(id+"F1.opExtrude","SWEPT_FACE",FACE,{"disambiguationData":[OSD([sQuery(id+"F0.wireOp",EDGE,"E1.top")])]}),makeQuery(id+"F3.opExtrude","SWEPT_FACE",FACE,{"disambiguationData":[OSD([sQuery(id+"F2.wireOp",EDGE,"E8.bottom")])]}),makeQuery(id+"F3.opExtrude","SWEPT_FACE",FACE,{"disambiguationData":[OSD([sQuery(id+"F2.wireOp",EDGE,"E7.bottom")])]})]}),makeQuery(id+"F5.opExtrude","SWEPT_FACE",FACE,{"disambiguationData":[OSD([sQuery(id+"F4.wireOp",EDGE,"E11.top")])]})]});
            var sketch = newSketch(context, id + "F8", { "sketchPlane" : qUnion([Q0])});
            skLineSegment(sketch, "E49", {"start": v(-37.25, 5) * mm, "end": v(-37.25, 14.75) * mm});
            skLineSegment(sketch, "E50", {"start": v(-37.25, 14.75) * mm, "end": v(-37.25, 16.75) * mm});
            skLineSegment(sketch, "E51", {"start": v(-37.25, 16.75) * mm, "end": v(-37.25, 26.5) * mm});
            skLineSegment(sketch, "E52", {"start": v(-37.25, 26.5) * mm, "end": v(-37.25, 28.5) * mm});
            skLineSegment(sketch, "E53", {"start": v(-37.25, 28.5) * mm, "end": v(-37.25, 38.25) * mm});
            skLineSegment(sketch, "E54", {"start": v(-37.25, 38.25) * mm, "end": v(-37.25, 40.25) * mm});
            skLineSegment(sketch, "E55", {"start": v(-37.25, 40.25) * mm, "end": v(-37.25, 50) * mm});
            skLineSegment(sketch, "E56", {"start": v(-37.25, 40.25) * mm, "end": v(-33.32, 40.25) * mm});
            skLineSegment(sketch, "E57", {"start": v(-37.25, 38.25) * mm, "end": v(-33.3, 38.25) * mm});
            skLineSegment(sketch, "E58", {"start": v(-36.71, 28.5) * mm, "end": v(-32.75, 28.5) * mm});
            skLineSegment(sketch, "E59", {"start": v(-37.25, 26.5) * mm, "end": v(-37.24, 26.5) * mm});
            skLineSegment(sketch, "E60", {"start": v(-37.25, 16.75) * mm, "end": v(-33.33, 16.75) * mm});
            skLineSegment(sketch, "E61", {"start": v(-37.25, 14.75) * mm, "end": v(-33.3, 14.75) * mm});
            skLineSegment(sketch, "E62.bottom", {"start": v(-37.25, 6.16) * mm, "end": v(-33.15, 15.08) * mm});
            skLineSegment(sketch, "E62.top", {"start": v(-36.68, 5) * mm, "end": v(-32.25, 14.66) * mm});
            skLineSegment(sketch, "E62.right", {"start": v(-32.75, 14.9) * mm, "end": v(-32.25, 14.66) * mm});
            skLineSegment(sketch, "E63", {"start": v(-32.7, 14.87) * mm, "end": v(-32.75, 14.76) * mm});
            skLineSegment(sketch, "E64.bottom", {"start": v(-33.2, 16.47) * mm, "end": v(-37.78, 26.47) * mm});
            skLineSegment(sketch, "E64.top", {"start": v(-32.29, 16.89) * mm, "end": v(-36.7, 26.5) * mm});
            skLineSegment(sketch, "E64.left", {"start": v(-32.75, 16.67) * mm, "end": v(-32.29, 16.89) * mm});
            skLineSegment(sketch, "E64.right", {"start": v(-37.32, 26.68) * mm, "end": v(-36.87, 26.89) * mm});
            skLineSegment(sketch, "E65", {"start": v(-32.74, 16.68) * mm, "end": v(-32.75, 16.7) * mm});
            skLineSegment(sketch, "E66", {"start": v(-37.32, 26.68) * mm, "end": v(-36.17, 24.16) * mm});
            skLineSegment(sketch, "E67.bottom", {"start": v(-37.77, 28.6) * mm, "end": v(-33.3, 38.25) * mm});
            skLineSegment(sketch, "E67.top", {"start": v(-36.71, 28.5) * mm, "end": v(-32.24, 38.16) * mm});
            skLineSegment(sketch, "E67.left", {"start": v(-37.77, 28.6) * mm, "end": v(-36.86, 28.18) * mm});
            skLineSegment(sketch, "E67.right", {"start": v(-33.15, 38.58) * mm, "end": v(-32.24, 38.16) * mm});
            skLineSegment(sketch, "E68", {"start": v(-37.31, 28.39) * mm, "end": v(-36.59, 29.96) * mm});
            skLineSegment(sketch, "E69", {"start": v(-32.7, 38.37) * mm, "end": v(-33.86, 35.86) * mm});
            skLineSegment(sketch, "E70.bottom", {"start": v(-33.18, 39.92) * mm, "end": v(-37.75, 49.93) * mm});
            skLineSegment(sketch, "E70.top", {"start": v(-32.27, 40.34) * mm, "end": v(-36.85, 50.34) * mm});
            skLineSegment(sketch, "E70.left", {"start": v(-32.75, 40.12) * mm, "end": v(-32.27, 40.34) * mm});
            skLineSegment(sketch, "E70.right", {"start": v(-37.75, 49.93) * mm, "end": v(-36.85, 50.34) * mm});
            skLineSegment(sketch, "E71", {"start": v(-32.72, 40.13) * mm, "end": v(-32.75, 40.2) * mm});
            skLineSegment(sketch, "E72", {"start": v(-37.3, 50.13) * mm, "end": v(-36.15, 47.62) * mm});
            skLineSegment(sketch, "E73", {"start": v(-32.75, 5) * mm, "end": v(-32.75, 14.75) * mm});
            skLineSegment(sketch, "E74", {"start": v(-37.25, 5) * mm, "end": v(-32.75, 5) * mm});
            skLineSegment(sketch, "E75.trimOffspring", {"start": v(-32.78, 16.75) * mm, "end": v(-33.46, 18.25) * mm});
            skLineSegment(sketch, "E76.trimOffspring", {"start": v(-32.75, 14.76) * mm, "end": v(-32.75, 50) * mm});
            skLineSegment(sketch, "E77.trimOffspring", {"start": v(-32.75, 14.75) * mm, "end": v(-33.86, 12.35) * mm});
            skLineSegment(sketch, "E78.trimOffspring", {"start": v(-32.77, 40.25) * mm, "end": v(-33.44, 41.7) * mm});
            skLineSegment(sketch, "E79.trimOffspring", {"start": v(-32.75, 14.75) * mm, "end": v(-32.75, 14.75) * mm});
            skLineSegment(sketch, "E80.trimOffspring", {"start": v(-32.78, 16.75) * mm, "end": v(-32.75, 16.75) * mm});
            skLineSegment(sketch, "E81.trimOffspring", {"start": v(-36.7, 26.5) * mm, "end": v(-32.75, 26.5) * mm});
            skLineSegment(sketch, "E82.trimOffspring", {"start": v(-32.75, 38.25) * mm, "end": v(-32.75, 38.25) * mm});
            skLineSegment(sketch, "E83.trimOffspring", {"start": v(-32.77, 40.25) * mm, "end": v(-32.75, 40.25) * mm});
            skLineSegment(sketch, "E84", {"start": v(-37.25, 6.16) * mm, "end": v(-37.25, 5) * mm});
            skLineSegment(sketch, "E85", {"start": v(-37.25, 5) * mm, "end": v(-36.68, 5) * mm});
            skSolve(sketch);
        }
        {
            var Q0;
            Q0=makeQuery(id+"F8.imprint","IMPRINT",FACE,{"disambiguationData":[TD([[makeQuery(id+"F8.imprint","IMPRINT",EDGE,{"derivedFrom":sQuery(id+"F8.wireOp",EDGE,"E50")}),1.0]])]});
            extrude(context, id + "F9", {"entities" : qUnion([Q0]), "operationType" : NewBodyOperationType.ADD, "oppositeDirection" : true, "depth" : 1.5 * mm, "offsetDistance" : 25 * mm});
        }
        {
            var Q0;
            Q0=makeQuery(id+"F5.boolean.opBoolean","MERGE",FACE,{"derivedFrom":[makeQuery(id+"F3.boolean.opBoolean","MERGE",FACE,{"derivedFrom":[makeQuery(id+"F1.opExtrude","SWEPT_FACE",FACE,{"disambiguationData":[OSD([sQuery(id+"F0.wireOp",EDGE,"E1.right")])]}),makeQuery(id+"F3.opExtrude","SWEPT_FACE",FACE,{"disambiguationData":[OSD([sQuery(id+"F2.wireOp",EDGE,"E9.left")])]}),makeQuery(id+"F3.opExtrude","SWEPT_FACE",FACE,{"disambiguationData":[OSD([sQuery(id+"F2.wireOp",EDGE,"E10.left")])]})]}),makeQuery(id+"F5.opExtrude","SWEPT_FACE",FACE,{"disambiguationData":[OSD([sQuery(id+"F4.wireOp",EDGE,"E11.right")])]})]});
            var sketch = newSketch(context, id + "F10", { "sketchPlane" : qUnion([Q0])});
            skLineSegment(sketch, "E86", {"start": v(44, 5) * mm, "end": v(44, 14.75) * mm});
            skLineSegment(sketch, "E87", {"start": v(44, 14.75) * mm, "end": v(44, 16.75) * mm});
            skLineSegment(sketch, "E88", {"start": v(44, 16.75) * mm, "end": v(44, 26.5) * mm});
            skLineSegment(sketch, "E89", {"start": v(44, 26.5) * mm, "end": v(44, 28.5) * mm});
            skLineSegment(sketch, "E90", {"start": v(44, 28.5) * mm, "end": v(44, 38.25) * mm});
            skLineSegment(sketch, "E91", {"start": v(44, 38.25) * mm, "end": v(44, 40.25) * mm});
            skLineSegment(sketch, "E92", {"start": v(44, 40.25) * mm, "end": v(44, 50) * mm});
            skLineSegment(sketch, "E93", {"start": v(44, 40.25) * mm, "end": v(47.93, 40.25) * mm});
            skLineSegment(sketch, "E94", {"start": v(44, 38.25) * mm, "end": v(47.95, 38.25) * mm});
            skLineSegment(sketch, "E95", {"start": v(44.54, 28.5) * mm, "end": v(48.5, 28.5) * mm});
            skLineSegment(sketch, "E96", {"start": v(44, 26.5) * mm, "end": v(44.01, 26.5) * mm});
            skLineSegment(sketch, "E97", {"start": v(44, 16.75) * mm, "end": v(47.92, 16.75) * mm});
            skLineSegment(sketch, "E98", {"start": v(44, 14.75) * mm, "end": v(47.95, 14.75) * mm});
            skLineSegment(sketch, "E99.bottom", {"start": v(44, 6.16) * mm, "end": v(48.1, 15.08) * mm});
            skLineSegment(sketch, "E99.top", {"start": v(44.57, 5) * mm, "end": v(49, 14.66) * mm});
            skLineSegment(sketch, "E99.right", {"start": v(48.5, 14.9) * mm, "end": v(49, 14.66) * mm});
            skLineSegment(sketch, "E100", {"start": v(48.55, 14.87) * mm, "end": v(48.5, 14.76) * mm});
            skLineSegment(sketch, "E101.bottom", {"start": v(48.05, 16.47) * mm, "end": v(43.47, 26.47) * mm});
            skLineSegment(sketch, "E101.top", {"start": v(48.96, 16.89) * mm, "end": v(44.56, 26.5) * mm});
            skLineSegment(sketch, "E101.left", {"start": v(48.5, 16.67) * mm, "end": v(48.96, 16.89) * mm});
            skLineSegment(sketch, "E101.right", {"start": v(43.93, 26.68) * mm, "end": v(44.38, 26.89) * mm});
            skLineSegment(sketch, "E102", {"start": v(48.5, 16.68) * mm, "end": v(48.5, 16.7) * mm});
            skLineSegment(sketch, "E103", {"start": v(43.93, 26.68) * mm, "end": v(45.08, 24.16) * mm});
            skLineSegment(sketch, "E104.bottom", {"start": v(43.48, 28.6) * mm, "end": v(47.95, 38.25) * mm});
            skLineSegment(sketch, "E104.top", {"start": v(44.54, 28.5) * mm, "end": v(49, 38.16) * mm});
            skLineSegment(sketch, "E104.left", {"start": v(43.48, 28.6) * mm, "end": v(44.4, 28.18) * mm});
            skLineSegment(sketch, "E104.right", {"start": v(48.1, 38.58) * mm, "end": v(49, 38.16) * mm});
            skLineSegment(sketch, "E105", {"start": v(43.94, 28.39) * mm, "end": v(44.66, 29.96) * mm});
            skLineSegment(sketch, "E106", {"start": v(48.56, 38.37) * mm, "end": v(47.4, 35.86) * mm});
            skLineSegment(sketch, "E107.bottom", {"start": v(48.07, 39.92) * mm, "end": v(43.5, 49.93) * mm});
            skLineSegment(sketch, "E107.top", {"start": v(48.98, 40.34) * mm, "end": v(44.4, 50.34) * mm});
            skLineSegment(sketch, "E107.left", {"start": v(48.5, 40.12) * mm, "end": v(48.98, 40.34) * mm});
            skLineSegment(sketch, "E107.right", {"start": v(43.5, 49.93) * mm, "end": v(44.4, 50.34) * mm});
            skLineSegment(sketch, "E108", {"start": v(48.53, 40.13) * mm, "end": v(48.5, 40.2) * mm});
            skLineSegment(sketch, "E109", {"start": v(43.95, 50.13) * mm, "end": v(45.1, 47.62) * mm});
            skLineSegment(sketch, "E110", {"start": v(48.5, 5) * mm, "end": v(48.5, 14.75) * mm});
            skLineSegment(sketch, "E111", {"start": v(44, 5) * mm, "end": v(48.5, 5) * mm});
            skLineSegment(sketch, "E112.trimOffspring", {"start": v(48.47, 16.75) * mm, "end": v(47.79, 18.25) * mm});
            skLineSegment(sketch, "E113.trimOffspring", {"start": v(48.5, 14.76) * mm, "end": v(48.5, 50) * mm});
            skLineSegment(sketch, "E114.trimOffspring", {"start": v(48.5, 14.75) * mm, "end": v(47.4, 12.35) * mm});
            skLineSegment(sketch, "E115.trimOffspring", {"start": v(48.48, 40.25) * mm, "end": v(47.8, 41.7) * mm});
            skLineSegment(sketch, "E116.trimOffspring", {"start": v(48.5, 14.75) * mm, "end": v(48.5, 14.75) * mm});
            skLineSegment(sketch, "E117.trimOffspring", {"start": v(48.47, 16.75) * mm, "end": v(48.5, 16.75) * mm});
            skLineSegment(sketch, "E118.trimOffspring", {"start": v(44.56, 26.5) * mm, "end": v(48.5, 26.5) * mm});
            skLineSegment(sketch, "E119.trimOffspring", {"start": v(48.5, 38.25) * mm, "end": v(48.5, 38.25) * mm});
            skLineSegment(sketch, "E120.trimOffspring", {"start": v(48.48, 40.25) * mm, "end": v(48.5, 40.25) * mm});
            skLineSegment(sketch, "E121", {"start": v(44, 6.16) * mm, "end": v(44, 5) * mm});
            skLineSegment(sketch, "E122", {"start": v(44, 5) * mm, "end": v(44.57, 5) * mm});
            skSolve(sketch);
        }
        {
            var Q0;
            Q0=makeQuery(id+"F10.imprint","IMPRINT",FACE,{"disambiguationData":[TD([[makeQuery(id+"F10.imprint","IMPRINT",EDGE,{"derivedFrom":sQuery(id+"F10.wireOp",EDGE,"E87")}),1.0]])]});
            extrude(context, id + "F11", {"entities" : qUnion([Q0]), "operationType" : NewBodyOperationType.ADD, "oppositeDirection" : true, "depth" : 1.5 * mm, "offsetDistance" : 25 * mm});
        }
        {
            var Q0;
            Q0=makeQuery(id+"F5.boolean.opBoolean","MERGE",FACE,{"derivedFrom":[makeQuery(id+"F3.boolean.opBoolean","MERGE",FACE,{"derivedFrom":[makeQuery(id+"F1.opExtrude","SWEPT_FACE",FACE,{"disambiguationData":[OSD([sQuery(id+"F0.wireOp",EDGE,"E4")])]}),makeQuery(id+"F3.opExtrude","SWEPT_FACE",FACE,{"disambiguationData":[OSD([sQuery(id+"F2.wireOp",EDGE,"E6.bottom")])]}),makeQuery(id+"F3.opExtrude","SWEPT_FACE",FACE,{"disambiguationData":[OSD([sQuery(id+"F2.wireOp",EDGE,"E10.bottom")])]})]}),makeQuery(id+"F5.opExtrude","SWEPT_FACE",FACE,{"disambiguationData":[OSD([sQuery(id+"F4.wireOp",EDGE,"E11.bottom")])]})]});
            var sketch = newSketch(context, id + "F12", { "sketchPlane" : qUnion([Q0])});
            skLineSegment(sketch, "E123", {"start": v(32.75, 5) * mm, "end": v(32.75, 14.75) * mm});
            skLineSegment(sketch, "E124", {"start": v(32.75, 14.75) * mm, "end": v(32.75, 16.75) * mm});
            skLineSegment(sketch, "E125", {"start": v(32.75, 16.75) * mm, "end": v(32.75, 26.5) * mm});
            skLineSegment(sketch, "E126", {"start": v(32.75, 26.5) * mm, "end": v(32.75, 28.5) * mm});
            skLineSegment(sketch, "E127", {"start": v(32.75, 28.5) * mm, "end": v(32.75, 38.25) * mm});
            skLineSegment(sketch, "E128", {"start": v(32.75, 38.25) * mm, "end": v(32.75, 40.25) * mm});
            skLineSegment(sketch, "E129", {"start": v(32.75, 40.25) * mm, "end": v(32.75, 50) * mm});
            skLineSegment(sketch, "E130", {"start": v(32.75, 40.25) * mm, "end": v(36.68, 40.25) * mm});
            skLineSegment(sketch, "E131", {"start": v(32.75, 38.25) * mm, "end": v(36.7, 38.25) * mm});
            skLineSegment(sketch, "E132", {"start": v(33.29, 28.5) * mm, "end": v(37.25, 28.5) * mm});
            skLineSegment(sketch, "E133", {"start": v(32.75, 26.5) * mm, "end": v(32.76, 26.5) * mm});
            skLineSegment(sketch, "E134", {"start": v(32.75, 16.75) * mm, "end": v(36.67, 16.75) * mm});
            skLineSegment(sketch, "E135", {"start": v(32.75, 14.75) * mm, "end": v(36.7, 14.75) * mm});
            skLineSegment(sketch, "E136.bottom", {"start": v(32.75, 6.16) * mm, "end": v(36.85, 15.08) * mm});
            skLineSegment(sketch, "E136.top", {"start": v(33.32, 5) * mm, "end": v(37.75, 14.66) * mm});
            skLineSegment(sketch, "E136.right", {"start": v(37.25, 14.9) * mm, "end": v(37.75, 14.66) * mm});
            skLineSegment(sketch, "E137", {"start": v(37.3, 14.87) * mm, "end": v(37.25, 14.76) * mm});
            skLineSegment(sketch, "E138.bottom", {"start": v(36.8, 16.47) * mm, "end": v(32.22, 26.47) * mm});
            skLineSegment(sketch, "E138.top", {"start": v(37.71, 16.89) * mm, "end": v(33.3, 26.5) * mm});
            skLineSegment(sketch, "E138.left", {"start": v(37.25, 16.67) * mm, "end": v(37.71, 16.89) * mm});
            skLineSegment(sketch, "E138.right", {"start": v(32.68, 26.68) * mm, "end": v(33.13, 26.89) * mm});
            skLineSegment(sketch, "E139", {"start": v(37.26, 16.68) * mm, "end": v(37.25, 16.7) * mm});
            skLineSegment(sketch, "E140", {"start": v(32.68, 26.68) * mm, "end": v(33.83, 24.16) * mm});
            skLineSegment(sketch, "E141.bottom", {"start": v(32.23, 28.6) * mm, "end": v(36.7, 38.25) * mm});
            skLineSegment(sketch, "E141.top", {"start": v(33.29, 28.5) * mm, "end": v(37.76, 38.16) * mm});
            skLineSegment(sketch, "E141.left", {"start": v(32.23, 28.6) * mm, "end": v(33.14, 28.18) * mm});
            skLineSegment(sketch, "E141.right", {"start": v(36.85, 38.58) * mm, "end": v(37.76, 38.16) * mm});
            skLineSegment(sketch, "E142", {"start": v(32.69, 28.39) * mm, "end": v(33.41, 29.96) * mm});
            skLineSegment(sketch, "E143", {"start": v(37.3, 38.37) * mm, "end": v(36.14, 35.86) * mm});
            skLineSegment(sketch, "E144.bottom", {"start": v(36.82, 39.92) * mm, "end": v(32.25, 49.93) * mm});
            skLineSegment(sketch, "E144.top", {"start": v(37.73, 40.34) * mm, "end": v(33.15, 50.34) * mm});
            skLineSegment(sketch, "E144.left", {"start": v(37.25, 40.12) * mm, "end": v(37.73, 40.34) * mm});
            skLineSegment(sketch, "E144.right", {"start": v(32.25, 49.93) * mm, "end": v(33.15, 50.34) * mm});
            skLineSegment(sketch, "E145", {"start": v(37.28, 40.13) * mm, "end": v(37.25, 40.2) * mm});
            skLineSegment(sketch, "E146", {"start": v(32.7, 50.13) * mm, "end": v(33.85, 47.62) * mm});
            skLineSegment(sketch, "E147", {"start": v(37.25, 5) * mm, "end": v(37.25, 14.75) * mm});
            skLineSegment(sketch, "E148", {"start": v(32.75, 5) * mm, "end": v(37.25, 5) * mm});
            skLineSegment(sketch, "E149.trimOffspring", {"start": v(37.22, 16.75) * mm, "end": v(36.54, 18.25) * mm});
            skLineSegment(sketch, "E150.trimOffspring", {"start": v(37.25, 14.76) * mm, "end": v(37.25, 50) * mm});
            skLineSegment(sketch, "E151.trimOffspring", {"start": v(37.25, 14.75) * mm, "end": v(36.14, 12.35) * mm});
            skLineSegment(sketch, "E152.trimOffspring", {"start": v(37.23, 40.25) * mm, "end": v(36.56, 41.7) * mm});
            skLineSegment(sketch, "E153.trimOffspring", {"start": v(37.25, 14.75) * mm, "end": v(37.25, 14.75) * mm});
            skLineSegment(sketch, "E154.trimOffspring", {"start": v(37.22, 16.75) * mm, "end": v(37.25, 16.75) * mm});
            skLineSegment(sketch, "E155.trimOffspring", {"start": v(33.3, 26.5) * mm, "end": v(37.25, 26.5) * mm});
            skLineSegment(sketch, "E156.trimOffspring", {"start": v(37.25, 38.25) * mm, "end": v(37.25, 38.25) * mm});
            skLineSegment(sketch, "E157.trimOffspring", {"start": v(37.23, 40.25) * mm, "end": v(37.25, 40.25) * mm});
            skLineSegment(sketch, "E158", {"start": v(32.75, 6.16) * mm, "end": v(32.75, 5) * mm});
            skLineSegment(sketch, "E159", {"start": v(32.75, 5) * mm, "end": v(33.32, 5) * mm});
            skSolve(sketch);
        }
        {
            var Q0;
            Q0=makeQuery(id+"F12.imprint","IMPRINT",FACE,{"disambiguationData":[TD([[makeQuery(id+"F12.imprint","IMPRINT",EDGE,{"derivedFrom":sQuery(id+"F12.wireOp",EDGE,"E124")}),1.0]])]});
            extrude(context, id + "F13", {"entities" : qUnion([Q0]), "operationType" : NewBodyOperationType.ADD, "oppositeDirection" : true, "depth" : 1.5 * mm, "offsetDistance" : 25 * mm});
        }
        {
            var Q0;
            Q0=makeQuery(id+"F1.opExtrude","SWEPT_BODY",BODY,{"disambiguationData":[OSD([sQuery(id+"F0.wireOp",EDGE,"E1.top"),sQuery(id+"F0.wireOp",EDGE,"E1.right"),sQuery(id+"F0.wireOp",EDGE,"E4"),sQuery(id+"F0.wireOp",EDGE,"E5")])]});
            transform(context, id + "F14", {"entities" : qUnion([Q0]), "transformType" : TransformType.TRANSLATION_3D, "dx" : 0 * mm, "dy" : -92.5 * mm, "dz" : 0 * mm, "makeCopy" : true});
        }
        {
            var Q0;
            Q0=makeQuery(id+"F1.opExtrude","SWEPT_BODY",BODY,{"disambiguationData":[OSD([sQuery(id+"F0.wireOp",EDGE,"E1.top"),sQuery(id+"F0.wireOp",EDGE,"E1.right"),sQuery(id+"F0.wireOp",EDGE,"E4"),sQuery(id+"F0.wireOp",EDGE,"E5")])]});
            deleteBodies(context, id + "F15", {"entities" : qUnion([Q0])});
        }
        {
            var Q0;
            Q0=qCreatedBy(makeId("Front.planeOp"),FACE);
            var sketch = newSketch(context, id + "F16", { "sketchPlane" : qUnion([Q0])});
            skLineSegment(sketch, "E160", {"start": v(0, 0) * mm, "end": v(-38.86, 0) * mm});
            skLineSegment(sketch, "E161", {"start": v(-38.86, 0) * mm, "end": v(-38.86, 15.5) * mm});
            skLineSegment(sketch, "E162", {"start": v(-38.86, 15.5) * mm, "end": v(-15.27, 15.5) * mm});
            skLineSegment(sketch, "E163", {"start": v(-38.86, 15.5) * mm, "end": v(-38.86, 57.1) * mm});
            skLineSegment(sketch, "E164", {"start": v(-38.86, 57.1) * mm, "end": v(-23.28, 57.1) * mm});
            skLineSegment(sketch, "E165", {"start": v(-23.28, 57.1) * mm, "end": v(-15.27, 15.5) * mm});
            skSolve(sketch);
        }
        {
            var Q0;
            Q0 = qSketchRegion(id + "F16", true);
            extrude(context, id + "F17", {"entities" : qUnion([Q0]), "operationType" : NewBodyOperationType.REMOVE, "depth" : 80 * mm, "offsetDistance" : 25 * mm});
        }
    });
